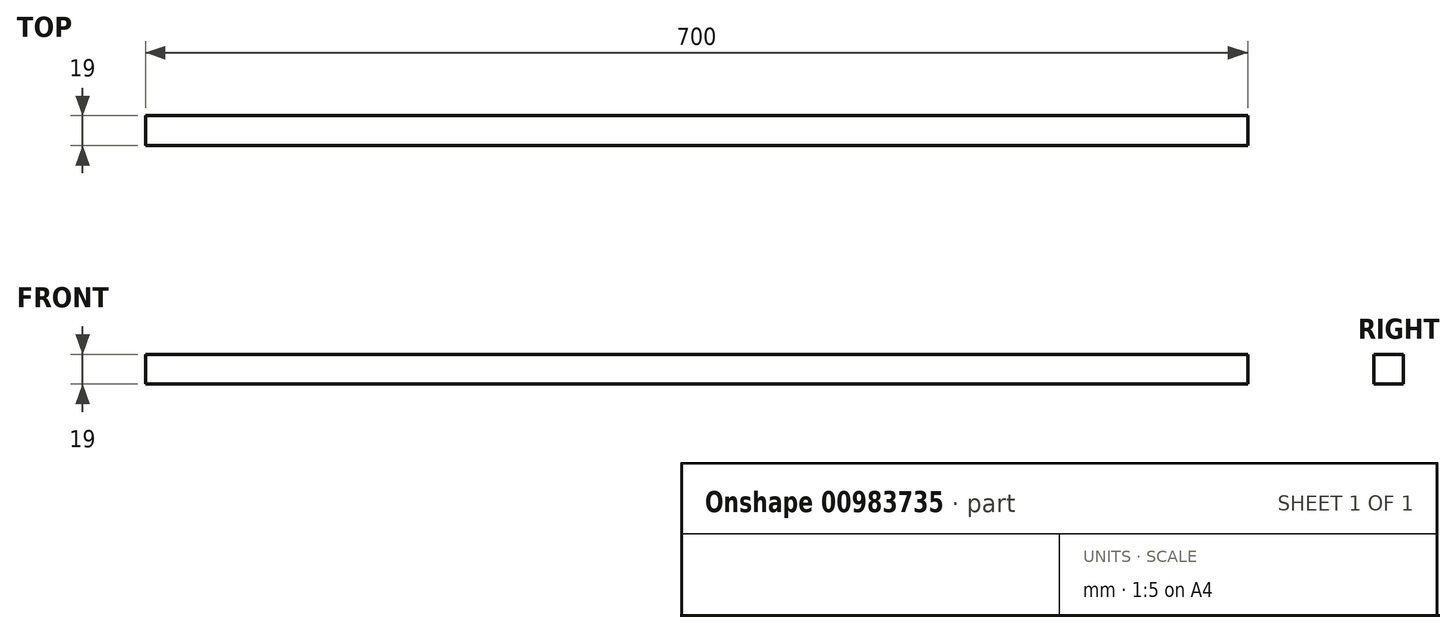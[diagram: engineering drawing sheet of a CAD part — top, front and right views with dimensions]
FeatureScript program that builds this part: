
annotation { "Feature Type Name" : "Feature", "Feature Type Description" : "" }
export const myFeature = defineFeature(function(context is Context, id is Id, definition is map)
    precondition{}
    {
        {
            var Q0;
            Q0=qCreatedBy(makeId("Front.planeOp"),FACE);
            var sketch = newSketch(context, id + "F0", { "sketchPlane" : qUnion([Q0])});
            skLineSegment(sketch, "E0.bottom", {"start": v(-46.37, 19) * mm, "end": v(653.63, 19) * mm});
            skLineSegment(sketch, "E0.top", {"start": v(-46.37, 0) * mm, "end": v(653.63, 0) * mm});
            skLineSegment(sketch, "E0.left", {"start": v(-46.37, 19) * mm, "end": v(-46.37, 0) * mm});
            skLineSegment(sketch, "E0.right", {"start": v(653.63, 19) * mm, "end": v(653.63, 0) * mm});
            skSolve(sketch);
        }
        {
            var Q0;
            Q0 = qSketchRegion(id + "F0", true);
            var Q1;
            Q1=makeQuery(id+"F0.imprint","IMPRINT",FACE,{"disambiguationData":[TD([[makeQuery(id+"F0.imprint","IMPRINT",EDGE,{"derivedFrom":sQuery(id+"F0.wireOp",EDGE,"E0.bottom")}),-1.0]])]});
            extrude(context, id + "F1", {"entities" : qUnion([Q0, Q1]), "depth" : 19 * mm, "offsetDistance" : 25.4 * mm});
        }
    });
